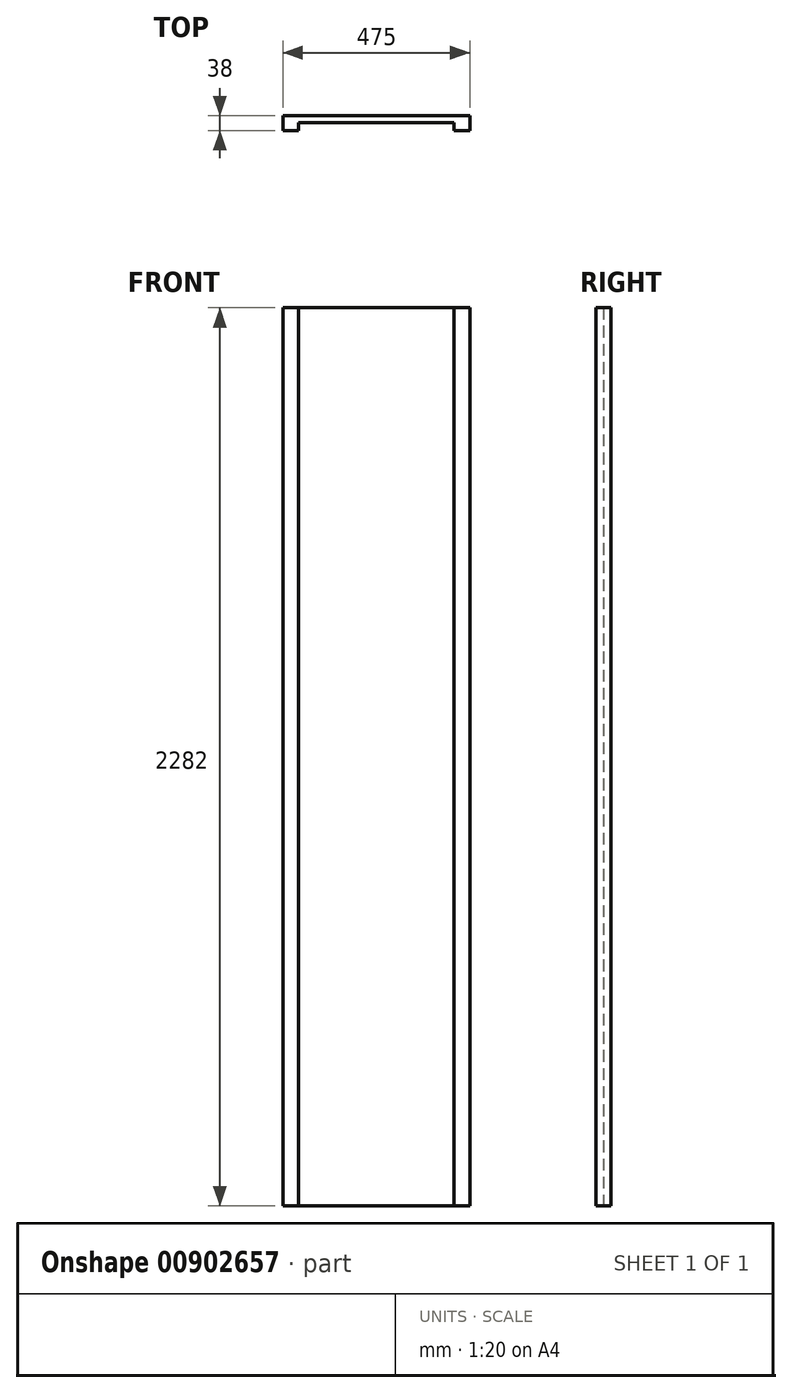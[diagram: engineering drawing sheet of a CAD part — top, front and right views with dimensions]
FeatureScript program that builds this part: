
annotation { "Feature Type Name" : "Feature", "Feature Type Description" : "" }
export const myFeature = defineFeature(function(context is Context, id is Id, definition is map)
    precondition{}
    {
        {
            var Q0;
            Q0=qCreatedBy(makeId("Front.planeOp"),FACE);
            var sketch = newSketch(context, id + "F0", { "sketchPlane" : qUnion([Q0])});
            skLineSegment(sketch, "E0.bottom", {"start": v(0, 0) * mm, "end": v(475, 0) * mm});
            skLineSegment(sketch, "E0.top", {"start": v(0, 2282) * mm, "end": v(475, 2282) * mm});
            skLineSegment(sketch, "E0.left", {"start": v(0, 0) * mm, "end": v(0, 2282) * mm});
            skLineSegment(sketch, "E0.right", {"start": v(475, 0) * mm, "end": v(475, 2282) * mm});
            skSolve(sketch);
        }
        {
            var Q0;
            Q0 = qSketchRegion(id + "F0", true);
            extrude(context, id + "F1", {"entities" : qUnion([Q0]), "depth" : 18 * mm, "offsetDistance" : 25 * mm});
        }
        {
            var Q0;
            Q0=makeQuery(id+"F1.opExtrude","SWEPT_FACE",FACE,{"disambiguationData":[OSD([sQuery(id+"F0.wireOp",EDGE,"E0.bottom")])]});
            var sketch = newSketch(context, id + "F2", { "sketchPlane" : qUnion([Q0])});
            skLineSegment(sketch, "E1.bottom", {"start": v(0, 18) * mm, "end": v(40, 18) * mm});
            skLineSegment(sketch, "E1.top", {"start": v(0, 38) * mm, "end": v(40, 38) * mm});
            skLineSegment(sketch, "E1.left", {"start": v(0, 18) * mm, "end": v(0, 38) * mm});
            skLineSegment(sketch, "E1.right", {"start": v(40, 18) * mm, "end": v(40, 38) * mm});
            skLineSegment(sketch, "E2.bottom", {"start": v(475, 18) * mm, "end": v(435, 18) * mm});
            skLineSegment(sketch, "E2.top", {"start": v(475, 38) * mm, "end": v(435, 38) * mm});
            skLineSegment(sketch, "E2.left", {"start": v(475, 18) * mm, "end": v(475, 38) * mm});
            skLineSegment(sketch, "E2.right", {"start": v(435, 18) * mm, "end": v(435, 38) * mm});
            skSolve(sketch);
        }
        {
            var Q0;
            Q0 = qSketchRegion(id + "F2", true);
            extrude(context, id + "F3", {"entities" : qUnion([Q0]), "operationType" : NewBodyOperationType.ADD, "oppositeDirection" : true, "depth" : 2282 * mm, "offsetDistance" : 25 * mm});
        }
    });
